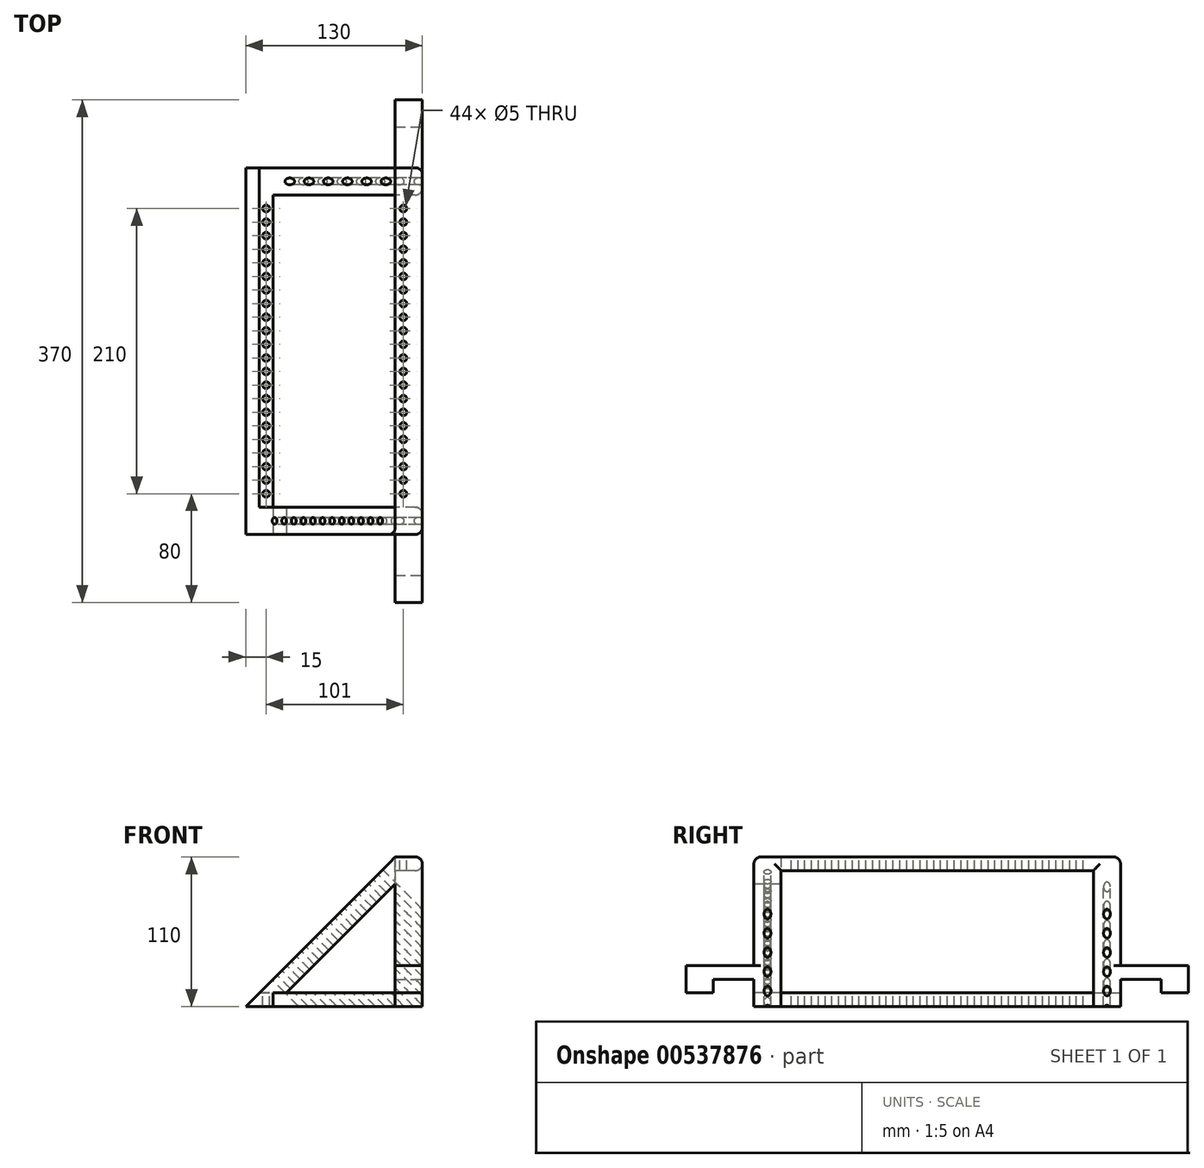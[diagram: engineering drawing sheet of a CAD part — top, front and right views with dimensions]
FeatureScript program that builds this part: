
annotation { "Feature Type Name" : "Feature", "Feature Type Description" : "" }
export const myFeature = defineFeature(function(context is Context, id is Id, definition is map)
    precondition{}
    {
        {
            var Q0;
            Q0=qCreatedBy(makeId("Right.planeOp"),FACE);
            var sketch = newSketch(context, id + "F0", { "sketchPlane" : qUnion([Q0])});
            skLineSegment(sketch, "E0", {"start": v(0, 0) * mm, "end": v(250, 0) * mm});
            skLineSegment(sketch, "E1", {"start": v(250, 0) * mm, "end": v(250, -100) * mm});
            skLineSegment(sketch, "E2", {"start": v(250, -100) * mm, "end": v(260, -100) * mm});
            skLineSegment(sketch, "E3", {"start": v(260, -100) * mm, "end": v(260, 10) * mm});
            skLineSegment(sketch, "E4", {"start": v(260, 10) * mm, "end": v(-10, 10) * mm});
            skLineSegment(sketch, "E5", {"start": v(-10, 10) * mm, "end": v(-10, -100) * mm});
            skLineSegment(sketch, "E6", {"start": v(-10, -100) * mm, "end": v(0, -100) * mm});
            skLineSegment(sketch, "E7", {"start": v(0, -100) * mm, "end": v(0, 0) * mm});
            skSolve(sketch);
        }
        {
            var Q0;
            Q0=makeQuery(id+"F0.imprint","IMPRINT",FACE,{"disambiguationData":[TD([[makeQuery(id+"F0.imprint","IMPRINT",EDGE,{"derivedFrom":sQuery(id+"F0.wireOp",EDGE,"E0")}),1.0]])]});
            extrude(context, id + "F1", {"entities" : qUnion([Q0]), "depth" : 10 * mm, "offsetDistance" : 25 * mm});
        }
        {
            var Q0;
            Q0=makeQuery(id+"F1.opExtrude","CAP_FACE",FACE,{"disambiguationData":[OSD([sQuery(id+"F0.wireOp",EDGE,"E0"),sQuery(id+"F0.wireOp",EDGE,"E1"),sQuery(id+"F0.wireOp",EDGE,"E2"),sQuery(id+"F0.wireOp",EDGE,"E3"),sQuery(id+"F0.wireOp",EDGE,"E4"),sQuery(id+"F0.wireOp",EDGE,"E5"),sQuery(id+"F0.wireOp",EDGE,"E6"),sQuery(id+"F0.wireOp",EDGE,"E7")])],"isStart":false});
            var sketch = newSketch(context, id + "F2", { "sketchPlane" : qUnion([Q0])});
            skLineSegment(sketch, "E8", {"start": v(-10, -100) * mm, "end": v(-10, -80) * mm});
            skLineSegment(sketch, "E9", {"start": v(-10, -80) * mm, "end": v(-40, -80) * mm});
            skLineSegment(sketch, "E10", {"start": v(-40, -80) * mm, "end": v(-40, -90) * mm});
            skLineSegment(sketch, "E11", {"start": v(-40, -90) * mm, "end": v(-60, -90) * mm});
            skLineSegment(sketch, "E12", {"start": v(-60, -90) * mm, "end": v(-60, -70) * mm});
            skLineSegment(sketch, "E13", {"start": v(-60, -70) * mm, "end": v(-10, -70) * mm});
            skLineSegment(sketch, "E14", {"start": v(-10, -70) * mm, "end": v(-10, -80) * mm});
            skLineSegment(sketch, "E15", {"start": v(260, -80) * mm, "end": v(290, -80) * mm});
            skLineSegment(sketch, "E16", {"start": v(290, -80) * mm, "end": v(290, -90) * mm});
            skLineSegment(sketch, "E17", {"start": v(290, -90) * mm, "end": v(310, -90) * mm});
            skLineSegment(sketch, "E18", {"start": v(310, -90) * mm, "end": v(310, -70) * mm});
            skLineSegment(sketch, "E19", {"start": v(310, -70) * mm, "end": v(260, -70) * mm});
            skLineSegment(sketch, "E20", {"start": v(260, -70) * mm, "end": v(260, -80) * mm});
            skSolve(sketch);
        }
        {
            var Q0;
            Q0=makeQuery(id+"F2.imprint","IMPRINT",FACE,{"disambiguationData":[TD([[makeQuery(id+"F2.imprint","IMPRINT",EDGE,{"derivedFrom":sQuery(id+"F2.wireOp",EDGE,"E9")}),-1.0]])]});
            var Q1;
            Q1=makeQuery(id+"F2.imprint","IMPRINT",FACE,{"disambiguationData":[TD([[makeQuery(id+"F2.imprint","IMPRINT",EDGE,{"derivedFrom":sQuery(id+"F2.wireOp",EDGE,"E15")}),1.0]])]});
            extrude(context, id + "F3", {"entities" : qUnion([Q0, Q1]), "operationType" : NewBodyOperationType.ADD, "depth" : -20 * mm, "offsetDistance" : 25 * mm});
        }
        {
            var Q0;
            Q0=makeQuery(id+"F3.boolean.opBoolean","MERGE",FACE,{"derivedFrom":[makeQuery(id+"F1.opExtrude","CAP_FACE",FACE,{"disambiguationData":[OSD([sQuery(id+"F0.wireOp",EDGE,"E0"),sQuery(id+"F0.wireOp",EDGE,"E1"),sQuery(id+"F0.wireOp",EDGE,"E2"),sQuery(id+"F0.wireOp",EDGE,"E3"),sQuery(id+"F0.wireOp",EDGE,"E4"),sQuery(id+"F0.wireOp",EDGE,"E5"),sQuery(id+"F0.wireOp",EDGE,"E6"),sQuery(id+"F0.wireOp",EDGE,"E7")])],"isStart":false}),makeQuery(id+"F3.opExtrude","CAP_FACE",FACE,{"disambiguationData":[OSD([sQuery(id+"F2.wireOp",EDGE,"E9"),sQuery(id+"F2.wireOp",EDGE,"E10"),sQuery(id+"F2.wireOp",EDGE,"E11"),sQuery(id+"F2.wireOp",EDGE,"E12"),sQuery(id+"F2.wireOp",EDGE,"E13"),sQuery(id+"F2.wireOp",EDGE,"E14")])],"isStart":true}),makeQuery(id+"F3.opExtrude","CAP_FACE",FACE,{"disambiguationData":[OSD([sQuery(id+"F2.wireOp",EDGE,"E15"),sQuery(id+"F2.wireOp",EDGE,"E16"),sQuery(id+"F2.wireOp",EDGE,"E17"),sQuery(id+"F2.wireOp",EDGE,"E18"),sQuery(id+"F2.wireOp",EDGE,"E19"),sQuery(id+"F2.wireOp",EDGE,"E20")])],"isStart":true})]});
            var sketch = newSketch(context, id + "F4", { "sketchPlane" : qUnion([Q0])});
            skLineSegment(sketch, "E21", {"start": v(-10, -70) * mm, "end": v(0, -70) * mm});
            skLineSegment(sketch, "E22", {"start": v(0, -70) * mm, "end": v(0, -80) * mm});
            skLineSegment(sketch, "E23", {"start": v(0, -80) * mm, "end": v(-10, -80) * mm});
            skLineSegment(sketch, "E24", {"start": v(-10, -80) * mm, "end": v(-10, -70) * mm});
            skLineSegment(sketch, "E25", {"start": v(260, -70) * mm, "end": v(250, -70) * mm});
            skLineSegment(sketch, "E26", {"start": v(250, -70) * mm, "end": v(250, -80) * mm});
            skLineSegment(sketch, "E27", {"start": v(250, -80) * mm, "end": v(260, -80) * mm});
            skLineSegment(sketch, "E28", {"start": v(260, -80) * mm, "end": v(260, -70) * mm});
            skSolve(sketch);
        }
        {
            var Q0;
            Q0=makeQuery(id+"F4.imprint","IMPRINT",FACE,{"disambiguationData":[TD([[makeQuery(id+"F4.imprint","IMPRINT",EDGE,{"derivedFrom":sQuery(id+"F4.wireOp",EDGE,"E21")}),-1.0]])]});
            var Q1;
            Q1=makeQuery(id+"F4.imprint","IMPRINT",FACE,{"disambiguationData":[TD([[makeQuery(id+"F4.imprint","IMPRINT",EDGE,{"derivedFrom":sQuery(id+"F4.wireOp",EDGE,"E25")}),1.0]])]});
            extrude(context, id + "F5", {"entities" : qUnion([Q0, Q1]), "operationType" : NewBodyOperationType.ADD, "depth" : -20 * mm, "offsetDistance" : 25 * mm});
        }
        {
            var Q0;
            Q0=makeQuery(id+"F5.boolean.opBoolean","MERGE",FACE,{"derivedFrom":[makeQuery(id+"F3.opExtrude","SWEPT_FACE",FACE,{"disambiguationData":[OSD([sQuery(id+"F2.wireOp",EDGE,"E15")])]}),makeQuery(id+"F5.opExtrude","SWEPT_FACE",FACE,{"disambiguationData":[OSD([sQuery(id+"F4.wireOp",EDGE,"E27")])]})]});
            var sketch = newSketch(context, id + "F6", { "sketchPlane" : qUnion([Q0])});
            skLineSegment(sketch, "E29.bottom", {"start": v(0, -250) * mm, "end": v(-10, -250) * mm});
            skLineSegment(sketch, "E29.top", {"start": v(0, -260) * mm, "end": v(-10, -260) * mm});
            skLineSegment(sketch, "E29.left", {"start": v(0, -250) * mm, "end": v(0, -260) * mm});
            skLineSegment(sketch, "E29.right", {"start": v(-10, -250) * mm, "end": v(-10, -260) * mm});
            skSolve(sketch);
        }
        {
            var Q0;
            Q0=makeQuery(id+"F6.imprint","IMPRINT",FACE,{"disambiguationData":[TD([[makeQuery(id+"F6.imprint","IMPRINT",EDGE,{"derivedFrom":sQuery(id+"F6.wireOp",EDGE,"E29.bottom")}),-1.0]])]});
            extrude(context, id + "F7", {"entities" : qUnion([Q0]), "operationType" : NewBodyOperationType.ADD, "depth" : 20 * mm, "offsetDistance" : 25 * mm});
        }
        {
            var Q0;
            Q0=makeQuery(id+"F5.boolean.opBoolean","MERGE",FACE,{"derivedFrom":[makeQuery(id+"F3.opExtrude","SWEPT_FACE",FACE,{"disambiguationData":[OSD([sQuery(id+"F2.wireOp",EDGE,"E9")])]}),makeQuery(id+"F5.opExtrude","SWEPT_FACE",FACE,{"disambiguationData":[OSD([sQuery(id+"F4.wireOp",EDGE,"E23")])]})]});
            var sketch = newSketch(context, id + "F8", { "sketchPlane" : qUnion([Q0])});
            skLineSegment(sketch, "E30.bottom", {"start": v(0, 10) * mm, "end": v(-10, 10) * mm});
            skLineSegment(sketch, "E30.top", {"start": v(0, 0) * mm, "end": v(-10, 0) * mm});
            skLineSegment(sketch, "E30.left", {"start": v(0, 10) * mm, "end": v(0, 0) * mm});
            skLineSegment(sketch, "E30.right", {"start": v(-10, 10) * mm, "end": v(-10, 0) * mm});
            skSolve(sketch);
        }
        {
            var Q0;
            Q0=makeQuery(id+"F8.imprint","IMPRINT",FACE,{"disambiguationData":[TD([[makeQuery(id+"F8.imprint","IMPRINT",EDGE,{"derivedFrom":sQuery(id+"F8.wireOp",EDGE,"E30.bottom")}),1.0]])]});
            extrude(context, id + "F9", {"entities" : qUnion([Q0]), "operationType" : NewBodyOperationType.ADD, "depth" : 20 * mm, "offsetDistance" : 25 * mm});
        }
        {
            var Q0;
            {var subQ0=sQuery(id+"F0.wireOp",EDGE,"E7");var subQ1=sQuery(id+"F0.wireOp",EDGE,"E5");var subQ2=sQuery(id+"F0.wireOp",EDGE,"E0");var subQ3=sQuery(id+"F0.wireOp",EDGE,"E3");var subQ4=sQuery(id+"F0.wireOp",EDGE,"E1");var subQ5=sQuery(id+"F0.wireOp",EDGE,"E4");Q0=makeQuery(id+"F5.boolean.opBoolean","SPLIT",FACE,{"disambiguationData":[TD([makeQuery(id+"F1.opExtrude","SWEPT_FACE",FACE,{"disambiguationData":[OSD([subQ2])]})])],"derivedFrom":makeQuery(id+"F1.opExtrude","CAP_FACE",FACE,{"disambiguationData":[OSD([subQ2,subQ4,sQuery(id+"F0.wireOp",EDGE,"E2"),subQ3,subQ5,subQ1,sQuery(id+"F0.wireOp",EDGE,"E6"),subQ0])],"isStart":true})});}
            var sketch = newSketch(context, id + "F10", { "sketchPlane" : qUnion([Q0])});
            skLineSegment(sketch, "E31", {"start": v(-260, 10) * mm, "end": v(-260, -70) * mm});
            skLineSegment(sketch, "E32", {"start": v(-260, -70) * mm, "end": v(-250, -70) * mm});
            skLineSegment(sketch, "E33", {"start": v(-250, -70) * mm, "end": v(-250, 0) * mm});
            skLineSegment(sketch, "E34", {"start": v(-250, 0) * mm, "end": v(0, 0) * mm});
            skLineSegment(sketch, "E35", {"start": v(0, 0) * mm, "end": v(0, -70) * mm});
            skLineSegment(sketch, "E36", {"start": v(0, -70) * mm, "end": v(10, -70) * mm});
            skLineSegment(sketch, "E37", {"start": v(10, -70) * mm, "end": v(10, 10) * mm});
            skLineSegment(sketch, "E38", {"start": v(10, 10) * mm, "end": v(-260, 10) * mm});
            skSolve(sketch);
        }
        {
            var Q0;
            Q0=makeQuery(id+"F10.imprint","IMPRINT",FACE,{"disambiguationData":[TD([[makeQuery(id+"F10.imprint","IMPRINT",EDGE,{"derivedFrom":sQuery(id+"F10.wireOp",EDGE,"E31")}),-1.0]])]});
            extrude(context, id + "F11", {"entities" : qUnion([Q0]), "operationType" : NewBodyOperationType.ADD, "depth" : 10 * mm, "offsetDistance" : 25 * mm});
        }
        {
            var Q0;
            {var subQ4=sQuery(id+"F0.wireOp",EDGE,"E5");var subQ5=sQuery(id+"F0.wireOp",EDGE,"E4");Q0=makeQuery(id+"F11.boolean.opBoolean","MERGE",FACE,{"derivedFrom":[makeQuery(id+"F3.boolean.opBoolean","SPLIT",FACE,{"disambiguationData":[TD([makeQuery(id+"F1.opExtrude","SWEPT_FACE",FACE,{"disambiguationData":[OSD([subQ5])]})])],"derivedFrom":makeQuery(id+"F1.opExtrude","SWEPT_FACE",FACE,{"disambiguationData":[OSD([subQ4])]})}),makeQuery(id+"F11.opExtrude","SWEPT_FACE",FACE,{"disambiguationData":[OSD([sQuery(id+"F10.wireOp",EDGE,"E37")])]})]});}
            var sketch = newSketch(context, id + "F12", { "sketchPlane" : qUnion([Q0])});
            skLineSegment(sketch, "E39", {"start": v(-10, 10) * mm, "end": v(-10, -100) * mm});
            skLineSegment(sketch, "E40", {"start": v(-10, -100) * mm, "end": v(-120, -100) * mm});
            skLineSegment(sketch, "E41", {"start": v(-120, -100) * mm, "end": v(-10, 10) * mm});
            skLineSegment(sketch, "E42", {"start": v(-10, -100) * mm, "end": v(-10, -90) * mm});
            skLineSegment(sketch, "E43", {"start": v(-10, -90) * mm, "end": v(-110, -90) * mm});
            skLineSegment(sketch, "E44", {"start": v(-110, -90) * mm, "end": v(-110, -100) * mm});
            skLineSegment(sketch, "E45", {"start": v(-110, -100) * mm, "end": v(-10, 0) * mm});
            skLineSegment(sketch, "E46", {"start": v(-110, -100) * mm, "end": v(-100, -100) * mm});
            skLineSegment(sketch, "E47", {"start": v(-100, -100) * mm, "end": v(-10, -10) * mm});
            skSolve(sketch);
        }
        {
            var Q0;
            {var subQ1=sQuery(id+"F12.wireOp",EDGE,"E39");var subQ3=sQuery(id+"F12.wireOp",EDGE,"E45");var subQ4=makeQuery(id+"F12.imprint","INTERSECT",VERTEX,{"derivedFrom":[subQ1,subQ3]});Q0=makeQuery(id+"F12.imprint","IMPRINT",FACE,{"disambiguationData":[TD([[makeQuery(id+"F12.imprint","IMPRINT",EDGE,{"disambiguationData":[TD([[subQ4,1.0]])],"derivedFrom":subQ3}),1.0]])]});}
            var Q1;
            {var subQ0=sQuery(id+"F12.wireOp",EDGE,"E42");Q1=makeQuery(id+"F12.imprint","IMPRINT",FACE,{"disambiguationData":[TD([[makeQuery(id+"F12.imprint","IMPRINT",EDGE,{"derivedFrom":subQ0}),1.0]])]});}
            var Q2;
            {var subQ0=sQuery(id+"F12.wireOp",EDGE,"E44");Q2=makeQuery(id+"F12.imprint","IMPRINT",FACE,{"disambiguationData":[TD([[makeQuery(id+"F12.imprint","IMPRINT",EDGE,{"derivedFrom":subQ0}),1.0]])]});}
            var Q3;
            {var subQ3=sQuery(id+"F12.wireOp",EDGE,"E44");Q3=makeQuery(id+"F12.imprint","IMPRINT",FACE,{"disambiguationData":[TD([[makeQuery(id+"F12.imprint","IMPRINT",EDGE,{"derivedFrom":subQ3}),-1.0]])]});}
            extrude(context, id + "F13", {"entities" : qUnion([Q0, Q1, Q2, Q3]), "operationType" : NewBodyOperationType.ADD, "depth" : -20 * mm, "offsetDistance" : 25 * mm});
        }
        {
            var Q0;
            {var subQ0=sQuery(id+"F12.wireOp",EDGE,"E45");var subQ1=sQuery(id+"F12.wireOp",EDGE,"E39");var subQ2=makeQuery(id+"F12.imprint","INTERSECT",VERTEX,{"derivedFrom":[subQ1,subQ0]});Q0=makeQuery(id+"F12.imprint","IMPRINT",FACE,{"disambiguationData":[TD([[makeQuery(id+"F12.imprint","IMPRINT",EDGE,{"disambiguationData":[TD([[subQ2,-1.0]])],"derivedFrom":subQ1}),-1.0]])]});}
            var Q1;
            {var subQ5=sQuery(id+"F12.wireOp",EDGE,"E46");Q1=makeQuery(id+"F12.imprint","IMPRINT",FACE,{"disambiguationData":[TD([[makeQuery(id+"F12.imprint","IMPRINT",EDGE,{"derivedFrom":subQ5}),1.0]])]});}
            extrude(context, id + "F14", {"entities" : qUnion([Q0, Q1]), "operationType" : NewBodyOperationType.ADD, "depth" : -20 * mm, "offsetDistance" : 25 * mm});
        }
        {
            var Q0;
            Q0=makeQuery(id+"F11.boolean.opBoolean","MERGE",FACE,{"derivedFrom":[makeQuery(id+"F9.boolean.opBoolean","MERGE",FACE,{"derivedFrom":[makeQuery(id+"F5.boolean.opBoolean","MERGE",FACE,{"derivedFrom":[makeQuery(id+"F1.opExtrude","SWEPT_FACE",FACE,{"disambiguationData":[OSD([sQuery(id+"F0.wireOp",EDGE,"E7")])]}),makeQuery(id+"F5.opExtrude","SWEPT_FACE",FACE,{"disambiguationData":[OSD([sQuery(id+"F4.wireOp",EDGE,"E22")])]})]}),makeQuery(id+"F9.opExtrude","SWEPT_FACE",FACE,{"disambiguationData":[OSD([sQuery(id+"F8.wireOp",EDGE,"E30.top")])]})]}),makeQuery(id+"F11.opExtrude","SWEPT_FACE",FACE,{"disambiguationData":[OSD([sQuery(id+"F10.wireOp",EDGE,"E35")])]})]});
            extrude(context, id + "F15", {"entities" : qUnion([Q0]), "operationType" : NewBodyOperationType.ADD, "depth" : 10 * mm, "offsetDistance" : 25 * mm});
        }
        {
            var Q0;
            {var subQ3=sQuery(id+"F0.wireOp",EDGE,"E4");var subQ4=sQuery(id+"F0.wireOp",EDGE,"E3");Q0=makeQuery(id+"F11.boolean.opBoolean","MERGE",FACE,{"derivedFrom":[makeQuery(id+"F3.boolean.opBoolean","SPLIT",FACE,{"disambiguationData":[TD([makeQuery(id+"F1.opExtrude","SWEPT_FACE",FACE,{"disambiguationData":[OSD([subQ3])]})])],"derivedFrom":makeQuery(id+"F1.opExtrude","SWEPT_FACE",FACE,{"disambiguationData":[OSD([subQ4])]})}),makeQuery(id+"F11.opExtrude","SWEPT_FACE",FACE,{"disambiguationData":[OSD([sQuery(id+"F10.wireOp",EDGE,"E31")])]})]});}
            var sketch = newSketch(context, id + "F16", { "sketchPlane" : qUnion([Q0])});
            skLineSegment(sketch, "E48", {"start": v(10, 10) * mm, "end": v(10, -100) * mm});
            skLineSegment(sketch, "E49", {"start": v(10, -100) * mm, "end": v(120, -100) * mm});
            skLineSegment(sketch, "E50", {"start": v(120, -100) * mm, "end": v(10, 10) * mm});
            skLineSegment(sketch, "E51", {"start": v(10, -100) * mm, "end": v(10, -90) * mm});
            skLineSegment(sketch, "E52", {"start": v(10, -90) * mm, "end": v(110, -90) * mm});
            skLineSegment(sketch, "E53", {"start": v(110, -90) * mm, "end": v(90, -90) * mm});
            skLineSegment(sketch, "E54", {"start": v(90, -90) * mm, "end": v(10, -10) * mm});
            skSolve(sketch);
        }
        {
            var Q0;
            {var subQ4=sQuery(id+"F16.wireOp",EDGE,"E53");Q0=makeQuery(id+"F16.imprint","IMPRINT",FACE,{"disambiguationData":[TD([[makeQuery(id+"F16.imprint","IMPRINT",EDGE,{"derivedFrom":subQ4}),-1.0]])]});}
            var Q1;
            {var subQ1=sQuery(id+"F16.wireOp",EDGE,"E49");Q1=makeQuery(id+"F16.imprint","IMPRINT",FACE,{"disambiguationData":[TD([[makeQuery(id+"F16.imprint","IMPRINT",EDGE,{"derivedFrom":subQ1}),1.0]])]});}
            extrude(context, id + "F17", {"entities" : qUnion([Q0, Q1]), "operationType" : NewBodyOperationType.ADD, "depth" : -20 * mm, "offsetDistance" : 25 * mm});
        }
        {
            var Q0;
            Q0=makeQuery(id+"F11.boolean.opBoolean","MERGE",FACE,{"derivedFrom":[makeQuery(id+"F7.boolean.opBoolean","MERGE",FACE,{"derivedFrom":[makeQuery(id+"F5.boolean.opBoolean","MERGE",FACE,{"derivedFrom":[makeQuery(id+"F1.opExtrude","SWEPT_FACE",FACE,{"disambiguationData":[OSD([sQuery(id+"F0.wireOp",EDGE,"E1")])]}),makeQuery(id+"F5.opExtrude","SWEPT_FACE",FACE,{"disambiguationData":[OSD([sQuery(id+"F4.wireOp",EDGE,"E26")])]})]}),makeQuery(id+"F7.opExtrude","SWEPT_FACE",FACE,{"disambiguationData":[OSD([sQuery(id+"F6.wireOp",EDGE,"E29.bottom")])]})]}),makeQuery(id+"F11.opExtrude","SWEPT_FACE",FACE,{"disambiguationData":[OSD([sQuery(id+"F10.wireOp",EDGE,"E33")])]})]});
            extrude(context, id + "F18", {"entities" : qUnion([Q0]), "operationType" : NewBodyOperationType.ADD, "depth" : 10 * mm, "offsetDistance" : 25 * mm});
        }
        {
            var Q0;
            Q0=makeQuery(id+"F18.boolean.opBoolean","MERGE",FACE,{"derivedFrom":[makeQuery(id+"F17.opExtrude","CAP_FACE",FACE,{"disambiguationData":[OSD([sQuery(id+"F16.wireOp",EDGE,"E48"),sQuery(id+"F16.wireOp",EDGE,"E49"),sQuery(id+"F16.wireOp",EDGE,"E50"),sQuery(id+"F16.wireOp",EDGE,"E51"),sQuery(id+"F16.wireOp",EDGE,"E52"),sQuery(id+"F16.wireOp",EDGE,"E54")])],"isStart":false}),makeQuery(id+"F18.opExtrude","CAP_FACE",FACE,{"disambiguationData":[OSD([sQuery(id+"F0.wireOp",EDGE,"E1"),sQuery(id+"F4.wireOp",EDGE,"E26"),sQuery(id+"F6.wireOp",EDGE,"E29.bottom"),sQuery(id+"F10.wireOp",EDGE,"E33")])],"isStart":false})]});
            var sketch = newSketch(context, id + "F19", { "sketchPlane" : qUnion([Q0])});
            skLineSegment(sketch, "E55", {"start": v(-90, -90) * mm, "end": v(-90, -100) * mm});
            skLineSegment(sketch, "E56", {"start": v(-90, -100) * mm, "end": v(-120, -100) * mm});
            skLineSegment(sketch, "E57", {"start": v(-120, -100) * mm, "end": v(-110, -90) * mm});
            skLineSegment(sketch, "E58", {"start": v(-110, -90) * mm, "end": v(-90, -90) * mm});
            skLineSegment(sketch, "E59", {"start": v(-90, -90) * mm, "end": v(-100, -90) * mm});
            skLineSegment(sketch, "E60", {"start": v(-100, -90) * mm, "end": v(-100, -100) * mm});
            skSolve(sketch);
        }
        {
            var Q0;
            Q0=makeQuery(id+"F1.opExtrude","CAP_EDGE",EDGE,{"disambiguationData":[OSD([sQuery(id+"F0.wireOp",EDGE,"E4")])],"isStart":false});
            var Q1;
            Q1=makeQuery(id+"F1.opExtrude","CAP_EDGE",EDGE,{"disambiguationData":[OSD([sQuery(id+"F0.wireOp",EDGE,"E0")])],"isStart":false});
            var Q2;
            Q2=makeQuery(id+"F15.opExtrude","CAP_EDGE",EDGE,{"disambiguationData":[OSD([sQuery(id+"F0.wireOp",EDGE,"E7")])],"isStart":false});
            var Q3;
            Q3=makeQuery(id+"F18.opExtrude","CAP_EDGE",EDGE,{"disambiguationData":[OSD([sQuery(id+"F0.wireOp",EDGE,"E1")])],"isStart":false});
            var Q4;
            {var subQ1=sQuery(id+"F0.wireOp",EDGE,"E5");var subQ2=sQuery(id+"F0.wireOp",EDGE,"E4");Q4=makeQuery(id+"F3.boolean.opBoolean","SPLIT",EDGE,{"disambiguationData":[TD([makeQuery(id+"F1.opExtrude","SWEPT_FACE",FACE,{"disambiguationData":[OSD([subQ2])]})])],"derivedFrom":makeQuery(id+"F1.opExtrude","CAP_EDGE",EDGE,{"disambiguationData":[OSD([subQ1])],"isStart":false})});}
            var Q5;
            {var subQ0=sQuery(id+"F0.wireOp",EDGE,"E4");var subQ1=sQuery(id+"F0.wireOp",EDGE,"E3");Q5=makeQuery(id+"F3.boolean.opBoolean","SPLIT",EDGE,{"disambiguationData":[TD([makeQuery(id+"F1.opExtrude","SWEPT_FACE",FACE,{"disambiguationData":[OSD([subQ0])]})])],"derivedFrom":makeQuery(id+"F1.opExtrude","CAP_EDGE",EDGE,{"disambiguationData":[OSD([subQ1])],"isStart":false})});}
            var Q6;
            Q6=makeQuery(id+"F11.boolean.opBoolean","MERGE",EDGE,{"derivedFrom":[makeQuery(id+"F1.opExtrude","SWEPT_EDGE",EDGE,{"disambiguationData":[OSD([sQuery(id+"F0.wireOp",EDGE,"E3"),sQuery(id+"F0.wireOp",EDGE,"E4")])]}),makeQuery(id+"F11.opExtrude","SWEPT_EDGE",EDGE,{"disambiguationData":[OSD([sQuery(id+"F10.wireOp",EDGE,"E31"),sQuery(id+"F10.wireOp",EDGE,"E38")])]})]});
            var Q7;
            Q7=makeQuery(id+"F11.boolean.opBoolean","MERGE",EDGE,{"derivedFrom":[makeQuery(id+"F1.opExtrude","SWEPT_EDGE",EDGE,{"disambiguationData":[OSD([sQuery(id+"F0.wireOp",EDGE,"E4"),sQuery(id+"F0.wireOp",EDGE,"E5")])]}),makeQuery(id+"F11.opExtrude","SWEPT_EDGE",EDGE,{"disambiguationData":[OSD([sQuery(id+"F10.wireOp",EDGE,"E37"),sQuery(id+"F10.wireOp",EDGE,"E38")])]})]});
            fillet(context, id + "F20", {"entities" : qUnion([Q0, Q1, Q2, Q3, Q4, Q5, Q6, Q7]), "radius" : 5 * mm, "tangentPropagation" : true, "allowEdgeOverflow" : false});
        }
        {
            var Q0;
            Q0=makeQuery(id+"F11.boolean.opBoolean","MERGE",FACE,{"derivedFrom":[makeQuery(id+"F1.opExtrude","SWEPT_FACE",FACE,{"disambiguationData":[OSD([sQuery(id+"F0.wireOp",EDGE,"E4")])]}),makeQuery(id+"F11.opExtrude","SWEPT_FACE",FACE,{"disambiguationData":[OSD([sQuery(id+"F10.wireOp",EDGE,"E38")])]})]});
            var sketch = newSketch(context, id + "F21", { "sketchPlane" : qUnion([Q0])});
            skLineSegment(sketch, "E61", {"start": v(-10, 10) * mm, "end": v(-10, 20) * mm});
            skLineSegment(sketch, "E62", {"start": v(-10, 20) * mm, "end": v(-4, 20) * mm});
            skLineSegment(sketch, "E63", {"start": v(-4, 20) * mm, "end": v(-4, 30) * mm});
            skLineSegment(sketch, "E64", {"start": v(-4, 30) * mm, "end": v(-4, 40) * mm});
            skLineSegment(sketch, "E65", {"start": v(-4, 40) * mm, "end": v(-4, 50) * mm});
            skLineSegment(sketch, "E66", {"start": v(-4, 50) * mm, "end": v(-4, 60) * mm});
            skLineSegment(sketch, "E67", {"start": v(-4, 60) * mm, "end": v(-4, 70) * mm});
            skLineSegment(sketch, "E68", {"start": v(-4, 70) * mm, "end": v(-4, 80) * mm});
            skLineSegment(sketch, "E69", {"start": v(-4, 80) * mm, "end": v(-4, 90) * mm});
            skLineSegment(sketch, "E70", {"start": v(-4, 90) * mm, "end": v(-4, 100) * mm});
            skLineSegment(sketch, "E71", {"start": v(-4, 100) * mm, "end": v(-4, 110) * mm});
            skLineSegment(sketch, "E72", {"start": v(-4, 110) * mm, "end": v(-4, 120) * mm});
            skLineSegment(sketch, "E73", {"start": v(-4, 120) * mm, "end": v(-4, 130) * mm});
            skLineSegment(sketch, "E74", {"start": v(-4, 130) * mm, "end": v(-4, 140) * mm});
            skLineSegment(sketch, "E75", {"start": v(-4, 140) * mm, "end": v(-4, 150) * mm});
            skLineSegment(sketch, "E76", {"start": v(-4, 150) * mm, "end": v(-4, 160) * mm});
            skLineSegment(sketch, "E77", {"start": v(-4, 160) * mm, "end": v(-4, 170) * mm});
            skLineSegment(sketch, "E78", {"start": v(-4, 170) * mm, "end": v(-4, 180) * mm});
            skLineSegment(sketch, "E79", {"start": v(-4, 180) * mm, "end": v(-4, 190) * mm});
            skLineSegment(sketch, "E80", {"start": v(-4, 190) * mm, "end": v(-4, 200) * mm});
            skLineSegment(sketch, "E81", {"start": v(-4, 200) * mm, "end": v(-4, 210) * mm});
            skLineSegment(sketch, "E82", {"start": v(-4, 210) * mm, "end": v(-4, 220) * mm});
            skLineSegment(sketch, "E83", {"start": v(-4, 220) * mm, "end": v(-4, 230) * mm});
            skLineSegment(sketch, "E84", {"start": v(-4, 230) * mm, "end": v(-4, 240) * mm});
            skSolve(sketch);
        }
        {
            var Q0;
            Q0=sQuery(id+"F21.wireOp",VERTEX,"E63.start");
            var Q1;
            Q1=sQuery(id+"F21.wireOp",VERTEX,"E64.start");
            var Q2;
            Q2=sQuery(id+"F21.wireOp",VERTEX,"E65.start");
            var Q3;
            Q3=sQuery(id+"F21.wireOp",VERTEX,"E66.start");
            var Q4;
            Q4=sQuery(id+"F21.wireOp",VERTEX,"E67.start");
            var Q5;
            Q5=sQuery(id+"F21.wireOp",VERTEX,"E68.start");
            var Q6;
            Q6=sQuery(id+"F21.wireOp",VERTEX,"E69.start");
            var Q7;
            Q7=sQuery(id+"F21.wireOp",VERTEX,"E70.start");
            var Q8;
            Q8=sQuery(id+"F21.wireOp",VERTEX,"E71.start");
            var Q9;
            Q9=sQuery(id+"F21.wireOp",VERTEX,"E72.start");
            var Q10;
            Q10=sQuery(id+"F21.wireOp",VERTEX,"E73.start");
            var Q11;
            Q11=sQuery(id+"F21.wireOp",VERTEX,"E74.start");
            var Q12;
            Q12=sQuery(id+"F21.wireOp",VERTEX,"E74.end");
            var Q13;
            Q13=sQuery(id+"F21.wireOp",VERTEX,"E75.end");
            var Q14;
            Q14=sQuery(id+"F21.wireOp",VERTEX,"E74.end");
            var Q15;
            Q15=sQuery(id+"F21.wireOp",VERTEX,"E76.end");
            var Q16;
            Q16=sQuery(id+"F21.wireOp",VERTEX,"E78.start");
            var Q17;
            Q17=sQuery(id+"F21.wireOp",VERTEX,"E79.start");
            var Q18;
            Q18=sQuery(id+"F21.wireOp",VERTEX,"E81.start");
            var Q19;
            Q19=sQuery(id+"F21.wireOp",VERTEX,"E82.start");
            var Q20;
            Q20=sQuery(id+"F21.wireOp",VERTEX,"E82.end");
            var Q21;
            Q21=sQuery(id+"F21.wireOp",VERTEX,"E83.end");
            var Q22;
            Q22=sQuery(id+"F21.wireOp",VERTEX,"E80.start");
            var Q23;
            Q23=makeQuery(id+"F1.opExtrude","SWEPT_BODY",BODY,{"disambiguationData":[OSD([sQuery(id+"F0.wireOp",EDGE,"E0"),sQuery(id+"F0.wireOp",EDGE,"E1"),sQuery(id+"F0.wireOp",EDGE,"E2"),sQuery(id+"F0.wireOp",EDGE,"E3"),sQuery(id+"F0.wireOp",EDGE,"E4"),sQuery(id+"F0.wireOp",EDGE,"E5"),sQuery(id+"F0.wireOp",EDGE,"E6"),sQuery(id+"F0.wireOp",EDGE,"E7")])]});
            hole(context, id + "F22", {"style" : HoleStyle.SIMPLE, "endStyle" : HoleEndStyle.THROUGH, "holeDiameter" : 5 * mm, "majorDiameter" : 5 * mm, "isTappedThrough" : true, "tappedDepth" : 12 * mm, "tapClearance" : 3, "locations" : qUnion([Q0, Q1, Q2, Q3, Q4, Q5, Q6, Q7, Q8, Q9, Q10, Q11, Q12, Q13, Q14, Q15, Q16, Q17, Q18, Q19, Q20, Q21, Q22]), "scope" : qUnion([Q23])});
        }
        {
            var Q0;
            {var subQ0=sQuery(id+"F19.wireOp",EDGE,"E57");Q0=makeQuery(id+"F19.imprint","IMPRINT",FACE,{"disambiguationData":[TD([[makeQuery(id+"F19.imprint","IMPRINT",EDGE,{"derivedFrom":subQ0}),-1.0]])]});}
            extrude(context, id + "F23", {"entities" : qUnion([Q0]), "operationType" : NewBodyOperationType.ADD, "depth" : 250 * mm, "offsetDistance" : 25 * mm});
        }
        {
            var Q0;
            Q0=makeQuery(id+"F23.opExtrude","SWEPT_FACE",FACE,{"disambiguationData":[OSD([sQuery(id+"F19.wireOp",EDGE,"E58")])]});
            var sketch = newSketch(context, id + "F24", { "sketchPlane" : qUnion([Q0])});
            skLineSegment(sketch, "E85", {"start": v(-105, 240) * mm, "end": v(-105, 230) * mm});
            skLineSegment(sketch, "E86", {"start": v(-105, 230) * mm, "end": v(-105, 220) * mm});
            skLineSegment(sketch, "E87", {"start": v(-105, 220) * mm, "end": v(-105, 210) * mm});
            skLineSegment(sketch, "E88", {"start": v(-105, 210) * mm, "end": v(-105, 200) * mm});
            skLineSegment(sketch, "E89", {"start": v(-105, 200) * mm, "end": v(-105, 190) * mm});
            skLineSegment(sketch, "E90", {"start": v(-105, 190) * mm, "end": v(-105, 180) * mm});
            skLineSegment(sketch, "E91", {"start": v(-105, 180) * mm, "end": v(-105, 170) * mm});
            skLineSegment(sketch, "E92", {"start": v(-105, 170) * mm, "end": v(-105, 160) * mm});
            skLineSegment(sketch, "E93", {"start": v(-105, 160) * mm, "end": v(-105, 150) * mm});
            skLineSegment(sketch, "E94", {"start": v(-105, 150) * mm, "end": v(-105, 140) * mm});
            skLineSegment(sketch, "E95", {"start": v(-105, 140) * mm, "end": v(-105, 130) * mm});
            skLineSegment(sketch, "E96", {"start": v(-105, 130) * mm, "end": v(-105, 120) * mm});
            skLineSegment(sketch, "E97", {"start": v(-105, 120) * mm, "end": v(-105, 110) * mm});
            skLineSegment(sketch, "E98", {"start": v(-105, 110) * mm, "end": v(-105, 100) * mm});
            skLineSegment(sketch, "E99", {"start": v(-105, 100) * mm, "end": v(-105, 90) * mm});
            skLineSegment(sketch, "E100", {"start": v(-105, 90) * mm, "end": v(-105, 80) * mm});
            skLineSegment(sketch, "E101", {"start": v(-105, 80) * mm, "end": v(-105, 70) * mm});
            skLineSegment(sketch, "E102", {"start": v(-105, 70) * mm, "end": v(-105, 60) * mm});
            skLineSegment(sketch, "E103", {"start": v(-105, 60) * mm, "end": v(-105, 50) * mm});
            skLineSegment(sketch, "E104", {"start": v(-105, 50) * mm, "end": v(-105, 40) * mm});
            skLineSegment(sketch, "E105", {"start": v(-105, 40) * mm, "end": v(-105, 30) * mm});
            skLineSegment(sketch, "E106", {"start": v(-105, 30) * mm, "end": v(-105, 20) * mm});
            skSolve(sketch);
        }
        {
            var Q0;
            Q0=sQuery(id+"F24.wireOp",VERTEX,"E106.end");
            var Q1;
            Q1=sQuery(id+"F24.wireOp",VERTEX,"E105.end");
            var Q2;
            Q2=sQuery(id+"F24.wireOp",VERTEX,"E104.end");
            var Q3;
            Q3=sQuery(id+"F24.wireOp",VERTEX,"E104.start");
            var Q4;
            Q4=sQuery(id+"F24.wireOp",VERTEX,"E103.start");
            var Q5;
            Q5=sQuery(id+"F24.wireOp",VERTEX,"E102.start");
            var Q6;
            Q6=sQuery(id+"F24.wireOp",VERTEX,"E100.end");
            var Q7;
            Q7=sQuery(id+"F24.wireOp",VERTEX,"E99.end");
            var Q8;
            Q8=sQuery(id+"F24.wireOp",VERTEX,"E98.end");
            var Q9;
            Q9=sQuery(id+"F24.wireOp",VERTEX,"E97.end");
            var Q10;
            Q10=sQuery(id+"F24.wireOp",VERTEX,"E96.end");
            var Q11;
            Q11=sQuery(id+"F24.wireOp",VERTEX,"E96.start");
            var Q12;
            Q12=sQuery(id+"F24.wireOp",VERTEX,"E95.start");
            var Q13;
            Q13=sQuery(id+"F24.wireOp",VERTEX,"E94.start");
            var Q14;
            Q14=sQuery(id+"F24.wireOp",VERTEX,"E93.start");
            var Q15;
            Q15=sQuery(id+"F24.wireOp",VERTEX,"E91.end");
            var Q16;
            Q16=sQuery(id+"F24.wireOp",VERTEX,"E91.start");
            var Q17;
            Q17=sQuery(id+"F24.wireOp",VERTEX,"E89.end");
            var Q18;
            Q18=sQuery(id+"F24.wireOp",VERTEX,"E89.start");
            var Q19;
            Q19=sQuery(id+"F24.wireOp",VERTEX,"E88.start");
            var Q20;
            Q20=sQuery(id+"F24.wireOp",VERTEX,"E87.start");
            var Q21;
            Q21=sQuery(id+"F24.wireOp",VERTEX,"E86.start");
            var Q22;
            Q22=makeQuery(id+"F1.opExtrude","SWEPT_BODY",BODY,{"disambiguationData":[OSD([sQuery(id+"F0.wireOp",EDGE,"E0"),sQuery(id+"F0.wireOp",EDGE,"E1"),sQuery(id+"F0.wireOp",EDGE,"E2"),sQuery(id+"F0.wireOp",EDGE,"E3"),sQuery(id+"F0.wireOp",EDGE,"E4"),sQuery(id+"F0.wireOp",EDGE,"E5"),sQuery(id+"F0.wireOp",EDGE,"E6"),sQuery(id+"F0.wireOp",EDGE,"E7")])]});
            hole(context, id + "F25", {"style" : HoleStyle.SIMPLE, "endStyle" : HoleEndStyle.THROUGH, "holeDiameter" : 5 * mm, "majorDiameter" : 5 * mm, "isTappedThrough" : true, "tappedDepth" : 12 * mm, "tapClearance" : 3, "locations" : qUnion([Q0, Q1, Q2, Q3, Q4, Q5, Q6, Q7, Q8, Q9, Q10, Q11, Q12, Q13, Q14, Q15, Q16, Q17, Q18, Q19, Q20, Q21]), "scope" : qUnion([Q22])});
        }
        {
            var Q0;
            Q0=makeQuery(id+"F23.boolean.opBoolean","MERGE",FACE,{"derivedFrom":[makeQuery(id+"F13.opExtrude","SWEPT_FACE",FACE,{"disambiguationData":[OSD([sQuery(id+"F12.wireOp",EDGE,"E41")])]}),makeQuery(id+"F17.opExtrude","SWEPT_FACE",FACE,{"disambiguationData":[OSD([sQuery(id+"F16.wireOp",EDGE,"E50")])]}),makeQuery(id+"F23.opExtrude","SWEPT_FACE",FACE,{"disambiguationData":[OSD([sQuery(id+"F19.wireOp",EDGE,"E57")])]})]});
            var sketch = newSketch(context, id + "F26", { "sketchPlane" : qUnion([Q0])});
            skLineSegment(sketch, "E107", {"start": v(-260, -155.56) * mm, "end": v(-250, -155.56) * mm});
            skLineSegment(sketch, "E108", {"start": v(-250, -155.56) * mm, "end": v(-250, -145.56) * mm});
            skLineSegment(sketch, "E109", {"start": v(-250, -145.56) * mm, "end": v(-250, -135.56) * mm});
            skLineSegment(sketch, "E110", {"start": v(-250, -135.56) * mm, "end": v(-250, -125.56) * mm});
            skLineSegment(sketch, "E111", {"start": v(-250, -125.56) * mm, "end": v(-250, -115.56) * mm});
            skLineSegment(sketch, "E112", {"start": v(-250, -115.56) * mm, "end": v(-250, -105.56) * mm});
            skLineSegment(sketch, "E113", {"start": v(-250, -105.56) * mm, "end": v(-250, -95.56) * mm});
            skLineSegment(sketch, "E114", {"start": v(-250, -95.56) * mm, "end": v(-250, -85.56) * mm});
            skLineSegment(sketch, "E115", {"start": v(-250, -85.56) * mm, "end": v(-250, -75.56) * mm});
            skLineSegment(sketch, "E116", {"start": v(-250, -75.56) * mm, "end": v(-250, -65.56) * mm});
            skLineSegment(sketch, "E117", {"start": v(-250, -65.56) * mm, "end": v(-250, -55.56) * mm});
            skLineSegment(sketch, "E118", {"start": v(-250, -55.56) * mm, "end": v(-250, -45.56) * mm});
            skLineSegment(sketch, "E119", {"start": v(-250, -45.56) * mm, "end": v(-250, -35.56) * mm});
            skLineSegment(sketch, "E120", {"start": v(-250, -35.56) * mm, "end": v(-250, -25.56) * mm});
            skLineSegment(sketch, "E121", {"start": v(-250, -25.56) * mm, "end": v(-250, -15.56) * mm});
            skPoint(sketch, "E121.endSnap0", {"position": v(-250, -7.07) * mm});
            skLineSegment(sketch, "E122", {"start": v(-250, -15.56) * mm, "end": v(0, -15.56) * mm, "construction": true});
            skLineSegment(sketch, "E123", {"start": v(0, -15.56) * mm, "end": v(0, -25.56) * mm});
            skLineSegment(sketch, "E124", {"start": v(0, -25.56) * mm, "end": v(0, -35.56) * mm});
            skLineSegment(sketch, "E125", {"start": v(0, -35.56) * mm, "end": v(0, -45.56) * mm});
            skLineSegment(sketch, "E126", {"start": v(0, -45.56) * mm, "end": v(0, -55.56) * mm});
            skLineSegment(sketch, "E127", {"start": v(0, -55.56) * mm, "end": v(0, -65.56) * mm});
            skLineSegment(sketch, "E128", {"start": v(0, -65.56) * mm, "end": v(0, -75.56) * mm});
            skLineSegment(sketch, "E129", {"start": v(0, -75.56) * mm, "end": v(0, -85.56) * mm});
            skLineSegment(sketch, "E130", {"start": v(0, -85.56) * mm, "end": v(0, -95.56) * mm});
            skLineSegment(sketch, "E131", {"start": v(0, -95.56) * mm, "end": v(0, -105.56) * mm});
            skLineSegment(sketch, "E132", {"start": v(0, -105.56) * mm, "end": v(0, -115.56) * mm});
            skLineSegment(sketch, "E133", {"start": v(0, -115.56) * mm, "end": v(0, -125.56) * mm});
            skLineSegment(sketch, "E134", {"start": v(0, -125.56) * mm, "end": v(0, -135.56) * mm});
            skLineSegment(sketch, "E135", {"start": v(0, -135.56) * mm, "end": v(0, -145.56) * mm});
            skLineSegment(sketch, "E136", {"start": v(0, -145.56) * mm, "end": v(0, -155.56) * mm});
            skSolve(sketch);
        }
        {
            var Q0;
            Q0=sQuery(id+"F26.wireOp",VERTEX,"E122.end");
            var Q1;
            Q1=sQuery(id+"F26.wireOp",VERTEX,"E123.end");
            var Q2;
            Q2=sQuery(id+"F26.wireOp",VERTEX,"E124.end");
            var Q3;
            Q3=sQuery(id+"F26.wireOp",VERTEX,"E125.end");
            var Q4;
            Q4=sQuery(id+"F26.wireOp",VERTEX,"E127.start");
            var Q5;
            Q5=sQuery(id+"F26.wireOp",VERTEX,"E128.start");
            var Q6;
            Q6=sQuery(id+"F26.wireOp",VERTEX,"E129.start");
            var Q7;
            Q7=sQuery(id+"F26.wireOp",VERTEX,"E130.start");
            var Q8;
            Q8=sQuery(id+"F26.wireOp",VERTEX,"E130.end");
            var Q9;
            Q9=sQuery(id+"F26.wireOp",VERTEX,"E131.end");
            var Q10;
            Q10=sQuery(id+"F26.wireOp",VERTEX,"E132.end");
            var Q11;
            Q11=sQuery(id+"F26.wireOp",VERTEX,"E133.end");
            var Q12;
            Q12=sQuery(id+"F26.wireOp",VERTEX,"E122.start");
            var Q13;
            Q13=sQuery(id+"F26.wireOp",VERTEX,"E121.start");
            var Q14;
            Q14=sQuery(id+"F26.wireOp",VERTEX,"E120.start");
            var Q15;
            Q15=sQuery(id+"F26.wireOp",VERTEX,"E119.start");
            var Q16;
            Q16=sQuery(id+"F26.wireOp",VERTEX,"E117.end");
            var Q17;
            Q17=sQuery(id+"F26.wireOp",VERTEX,"E116.end");
            var Q18;
            Q18=sQuery(id+"F26.wireOp",VERTEX,"E115.end");
            var Q19;
            Q19=sQuery(id+"F26.wireOp",VERTEX,"E114.end");
            var Q20;
            Q20=sQuery(id+"F26.wireOp",VERTEX,"E113.end");
            var Q21;
            Q21=sQuery(id+"F26.wireOp",VERTEX,"E113.start");
            var Q22;
            Q22=sQuery(id+"F26.wireOp",VERTEX,"E112.start");
            var Q23;
            Q23=sQuery(id+"F26.wireOp",VERTEX,"E111.start");
            var Q24;
            Q24=makeQuery(id+"F1.opExtrude","SWEPT_BODY",BODY,{"disambiguationData":[OSD([sQuery(id+"F0.wireOp",EDGE,"E0"),sQuery(id+"F0.wireOp",EDGE,"E1"),sQuery(id+"F0.wireOp",EDGE,"E2"),sQuery(id+"F0.wireOp",EDGE,"E3"),sQuery(id+"F0.wireOp",EDGE,"E4"),sQuery(id+"F0.wireOp",EDGE,"E5"),sQuery(id+"F0.wireOp",EDGE,"E6"),sQuery(id+"F0.wireOp",EDGE,"E7")])]});
            hole(context, id + "F27", {"style" : HoleStyle.SIMPLE, "endStyle" : HoleEndStyle.THROUGH, "holeDiameter" : 5 * mm, "majorDiameter" : 5 * mm, "isTappedThrough" : true, "tappedDepth" : 12 * mm, "tapClearance" : 3, "locations" : qUnion([Q0, Q1, Q2, Q3, Q4, Q5, Q6, Q7, Q8, Q9, Q10, Q11, Q12, Q13, Q14, Q15, Q16, Q17, Q18, Q19, Q20, Q21, Q22, Q23]), "scope" : qUnion([Q24])});
        }
    });
